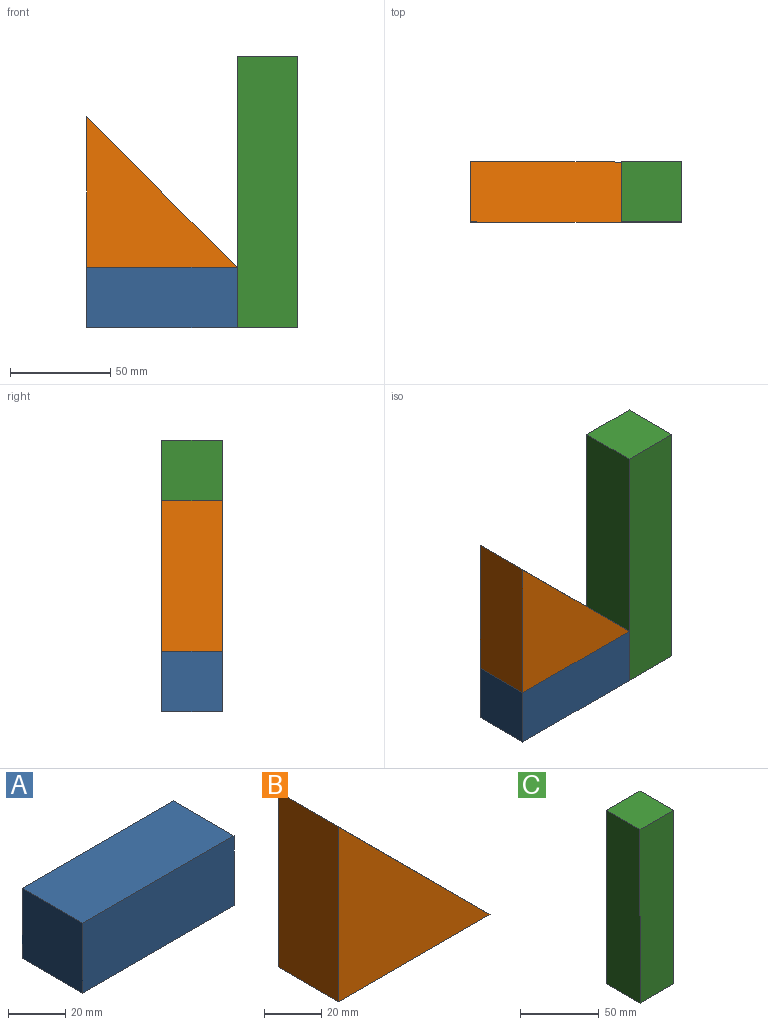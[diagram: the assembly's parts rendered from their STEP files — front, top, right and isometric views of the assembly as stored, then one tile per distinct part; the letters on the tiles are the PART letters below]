
ASSEMBLY  parts=3 mates=7
PART A: 6 faces, bbox 75x30x30 mm
  f0: plane 30x30mm, normal (-1,0,0), area 900mm2, adj f1,f3,f4,f5
  f1: plane 75x30mm, normal (0,0,-1), area 2250mm2, adj f0,f2,f4,f5
  f2: plane 30x30mm, normal (1,0,0), area 900mm2, adj f1,f3,f4,f5
  f3: plane 75x30mm, normal (0,0,1), area 2250mm2, adj f0,f2,f4,f5
  f4: plane 75x30mm, normal (0,-1,0), area 2250mm2, adj f0,f1,f2,f3
  f5: plane 75x30mm, normal (0,1,0), area 2250mm2, adj f0,f1,f2,f3
PART B: 5 faces, bbox 75x30x75 mm
  f0: plane 75x30mm, normal (-1,0,0), area 2250mm2, adj f1,f2,f3,f4
  f1: plane 75x30mm, normal (0,0,-1), area 2250mm2, adj f0,f2,f3,f4
  f2: plane 75x75mm, normal (0.71,0,0.71), area 3182mm2, adj f0,f1,f3,f4
  f3: plane 75x75mm, normal (0,-1,0), area 2812.5mm2, adj f0,f1,f2
  f4: plane 75x75mm, normal (0,1,0), area 2812.5mm2, adj f0,f1,f2
PART C: 6 faces, bbox 30x30x135 mm
  f0: plane 135x30mm, normal (-1,0,0), area 4050mm2, adj f1,f3,f4,f5
  f1: plane 30x30mm, normal (0,0,-1), area 900mm2, adj f0,f2,f4,f5
  f2: plane 135x30mm, normal (1,0,0), area 4050mm2, adj f1,f3,f4,f5
  f3: plane 30x30mm, normal (0,0,1), area 900mm2, adj f0,f2,f4,f5
  f4: plane 135x30mm, normal (0,-1,0), area 4050mm2, adj f0,f1,f2,f3
  f5: plane 135x30mm, normal (0,1,0), area 4050mm2, adj f0,f1,f2,f3
PLACE A t=(29.51,-3.57,-34.02)mm
PLACE B t=(29.51,-3.57,-4.02)mm
PLACE C t=(104.51,-3.57,-34.02)mm
MATE planar C.f0 <-> A.f2  axis (-1,0,0) through (104.51,-3.57,33.48)mm
MATE planar B.f3 <-> C.f4  axis (0,-1,0) through (54.51,-33.57,20.98)mm
MATE planar A.f1 <-> C.f1  axis (0,0,-1) through (67.01,-18.57,-34.02)mm
MATE planar B.f0 <-> A.f0  axis (-1,0,0) through (29.51,-18.57,33.48)mm
MATE planar C.f0 <-> A.f2  axis (-1,0,0) through (104.51,-3.57,100.98)mm
MATE planar C.f4 <-> A.f4  axis (0,-1,0) through (119.51,-33.57,33.48)mm
MATE planar A.f3 <-> B.f1  axis (0,0,1) through (29.51,-33.57,-4.02)mm
